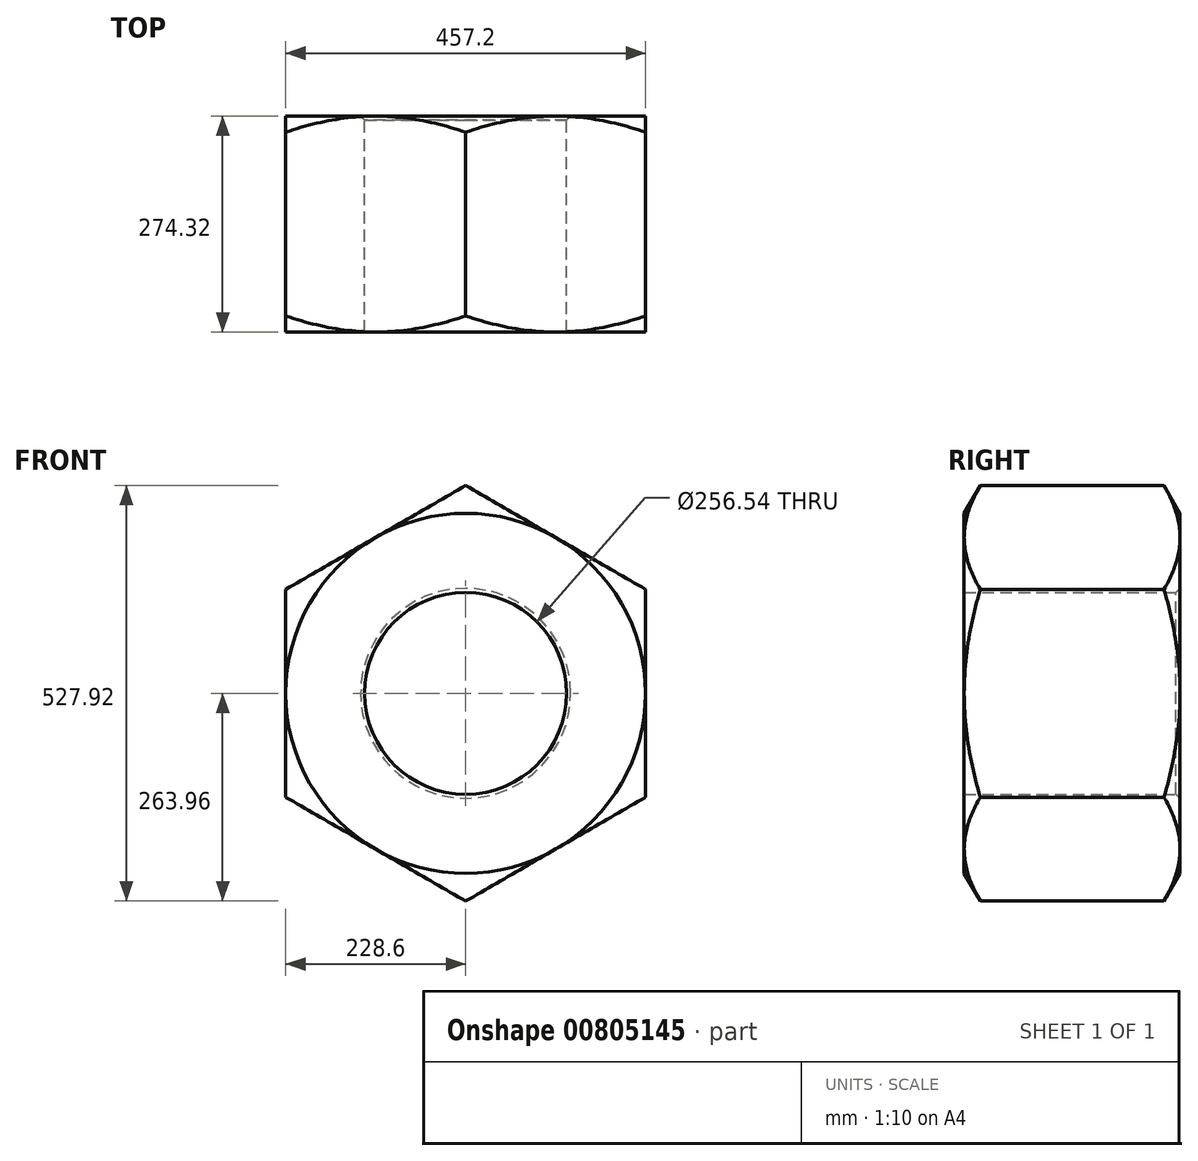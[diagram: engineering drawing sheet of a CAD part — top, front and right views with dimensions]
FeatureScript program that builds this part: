
annotation { "Feature Type Name" : "Feature", "Feature Type Description" : "" }
export const myFeature = defineFeature(function(context is Context, id is Id, definition is map)
    precondition{}
    {
        {
            var Q0;
            Q0=qCreatedBy(makeId("Front.planeOp"),FACE);
            var sketch = newSketch(context, id + "F0", { "sketchPlane" : qUnion([Q0])});
            skCircle(sketch, "E0.cCircle", {"center": v(0, 0) * mm, "radius": 228.6 * mm, "construction": true});
            skLineSegment(sketch, "E0.0", {"start": v(228.6, 131.98) * mm, "end": v(228.6, -131.98) * mm});
            skLineSegment(sketch, "E0.1", {"start": v(228.6, -131.98) * mm, "end": v(0, -263.96) * mm});
            skLineSegment(sketch, "E0.2", {"start": v(0, -263.96) * mm, "end": v(-228.6, -131.98) * mm});
            skLineSegment(sketch, "E0.3", {"start": v(-228.6, -131.98) * mm, "end": v(-228.6, 131.98) * mm});
            skLineSegment(sketch, "E0.4", {"start": v(-228.6, 131.98) * mm, "end": v(0, 263.96) * mm});
            skLineSegment(sketch, "E0.5", {"start": v(0, 263.96) * mm, "end": v(228.6, 131.98) * mm});
            skPoint(sketch, "E0.0.midPoint", {"position": v(228.6, 0) * mm});
            skCircle(sketch, "E1", {"center": v(0, 0) * mm, "radius": 128.27 * mm});
            skSolve(sketch);
        }
        {
            var Q0;
            Q0=makeQuery(id+"F0.imprint","IMPRINT",FACE,{"disambiguationData":[TD([[makeQuery(id+"F0.imprint","IMPRINT",EDGE,{"derivedFrom":sQuery(id+"F0.wireOp",EDGE,"E0.0")}),-1.0]])]});
            extrude(context, id + "F1", {"entities" : qUnion([Q0]), "depth" : 274.32 * mm, "offsetDistance" : 25.4 * mm});
        }
        {
            var Q0;
            Q0=makeQuery(id+"F1.opExtrude","SWEPT_BODY",BODY,{"disambiguationData":[OSD([sQuery(id+"F0.wireOp",EDGE,"E0.0"),sQuery(id+"F0.wireOp",EDGE,"E0.1"),sQuery(id+"F0.wireOp",EDGE,"E0.2"),sQuery(id+"F0.wireOp",EDGE,"E0.3"),sQuery(id+"F0.wireOp",EDGE,"E0.4"),sQuery(id+"F0.wireOp",EDGE,"E0.5"),sQuery(id+"F0.wireOp",EDGE,"E1")])]});
            transform(context, id + "F2", {"entities" : qUnion([Q0]), "transformType" : TransformType.TRANSLATION_3D, "dx" : 0 * mm, "dy" : 0 * mm, "dz" : 0 * mm, "makeCopy" : true});
        }
        {
            var Q0;
            Q0=makeQuery(id+"F1.opExtrude","SWEPT_BODY",BODY,{"disambiguationData":[OSD([sQuery(id+"F0.wireOp",EDGE,"E0.0"),sQuery(id+"F0.wireOp",EDGE,"E0.1"),sQuery(id+"F0.wireOp",EDGE,"E0.2"),sQuery(id+"F0.wireOp",EDGE,"E0.3"),sQuery(id+"F0.wireOp",EDGE,"E0.4"),sQuery(id+"F0.wireOp",EDGE,"E0.5"),sQuery(id+"F0.wireOp",EDGE,"E1")])]});
            deleteBodies(context, id + "F3", {"entities" : qUnion([Q0])});
        }
        {
            var Q0;
            Q0=qCreatedBy(makeId("Top.planeOp"),FACE);
            var sketch = newSketch(context, id + "F4", { "sketchPlane" : qUnion([Q0])});
            skLineSegment(sketch, "E2", {"start": v(0, -274.32) * mm, "end": v(0, 0) * mm, "construction": true});
            skLineSegment(sketch, "E3", {"start": v(0, 0) * mm, "end": v(0, -137.16) * mm, "construction": true});
            skLineSegment(sketch, "E4", {"start": v(0, -137.16) * mm, "end": v(229.44, -137.16) * mm, "construction": true});
            skLineSegment(sketch, "E5", {"start": v(228.6, -274.32) * mm, "end": v(435.95, -274.32) * mm});
            skLineSegment(sketch, "E6", {"start": v(435.95, -274.32) * mm, "end": v(435.95, -154.6) * mm});
            skLineSegment(sketch, "E7", {"start": v(435.95, -154.6) * mm, "end": v(228.6, -274.32) * mm});
            skLineSegment(sketch, "E8.MirrorCS", {"start": v(435.95, -119.72) * mm, "end": v(228.6, 0) * mm});
            skLineSegment(sketch, "E9.MirrorCS", {"start": v(228.6, 0) * mm, "end": v(435.95, 0) * mm});
            skLineSegment(sketch, "E10.MirrorCS", {"start": v(435.95, 0) * mm, "end": v(435.95, -119.72) * mm});
            skSolve(sketch);
        }
        {
            var Q0;
            Q0=makeQuery(id+"F4.imprint","IMPRINT",FACE,{"disambiguationData":[TD([[makeQuery(id+"F4.imprint","IMPRINT",EDGE,{"derivedFrom":sQuery(id+"F4.wireOp",EDGE,"E5")}),1.0]])]});
            var Q1;
            Q1=makeQuery(id+"F4.imprint","IMPRINT",FACE,{"disambiguationData":[TD([[makeQuery(id+"F4.imprint","IMPRINT",EDGE,{"derivedFrom":sQuery(id+"F4.wireOp",EDGE,"E8.MirrorCS")}),-1.0]])]});
            var Q2;
            Q2=sQuery(id+"F4.wireOp",EDGE,"E2");
            revolve(context, id + "F5", {"operationType" : NewBodyOperationType.REMOVE, "surfaceOperationType" : NewSurfaceOperationType.NEW, "entities" : qUnion([Q0, Q1]), "axis" : qUnion([Q2]), "revolveType" : RevolveType.FULL, "oppositeDirection" : true});
        }
        {
            var Q0;
            Q0=makeQuery(id+"F2.opPattern","COPY",EDGE,{"derivedFrom":makeQuery(id+"F1.opExtrude","CAP_EDGE",EDGE,{"disambiguationData":[OSD([sQuery(id+"F0.wireOp",EDGE,"E1")])],"isStart":true}),"instanceName":"1"});
            chamfer(context, id + "F6", {"entities" : qUnion([Q0]), "width" : 5.08 * mm, "tangentPropagation" : true});
        }
    });
